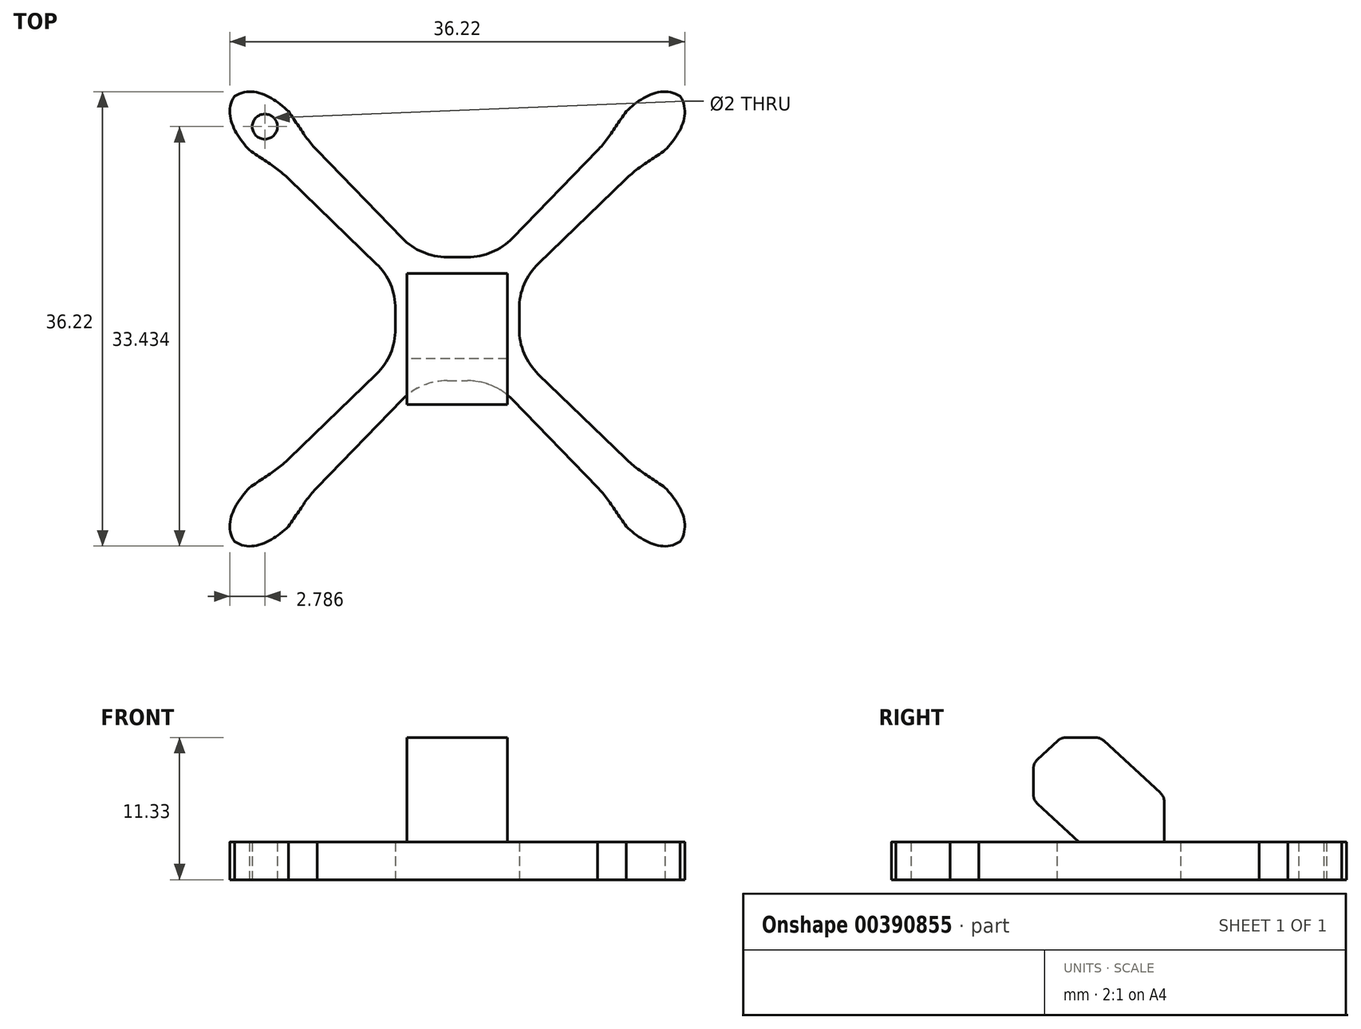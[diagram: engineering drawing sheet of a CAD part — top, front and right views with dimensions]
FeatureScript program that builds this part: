
annotation { "Feature Type Name" : "Feature", "Feature Type Description" : "" }
export const myFeature = defineFeature(function(context is Context, id is Id, definition is map)
    precondition{}
    {
        {
            var Q0;
            Q0=qCreatedBy(makeId("Top.planeOp"),FACE);
            var sketch = newSketch(context, id + "F0", { "sketchPlane" : qUnion([Q0])});
            skLineSegment(sketch, "E0.bottom", {"start": v(-17, -17) * mm, "end": v(17, -17) * mm, "construction": true});
            skLineSegment(sketch, "E0.top", {"start": v(-17, 17) * mm, "end": v(17, 17) * mm, "construction": true});
            skLineSegment(sketch, "E0.left", {"start": v(-17, -17) * mm, "end": v(-17, 17) * mm, "construction": true});
            skLineSegment(sketch, "E0.right", {"start": v(17, -17) * mm, "end": v(17, 17) * mm, "construction": true});
            skPoint(sketch, "E0.middle", {"position": v(0, 0) * mm});
            skLineSegment(sketch, "E1", {"start": v(-17, 17) * mm, "end": v(17, -17) * mm, "construction": true});
            skLineSegment(sketch, "E2", {"start": v(-17, -17) * mm, "end": v(17, 17) * mm, "construction": true});
            skLineSegment(sketch, "E3.bottom", {"start": v(-2.92, -4.92) * mm, "end": v(2.92, -4.92) * mm});
            skLineSegment(sketch, "E3.top", {"start": v(-2.92, 4.92) * mm, "end": v(2.92, 4.92) * mm});
            skLineSegment(sketch, "E3.left", {"start": v(-4.92, -2.92) * mm, "end": v(-4.92, 2.92) * mm});
            skLineSegment(sketch, "E3.right", {"start": v(4.92, -2.92) * mm, "end": v(4.92, 2.92) * mm});
            skPoint(sketch, "E4.visualSharp", {"position": v(-4.92, 4.92) * mm});
            skArc(sketch, "E4.filletArc", {"start": v(-2.92, 4.92) * mm, "mid": v(-4.34, 4.34) * mm, "end": v(-4.92, 2.92) * mm});
            skPoint(sketch, "E5.visualSharp", {"position": v(-4.92, -4.92) * mm});
            skArc(sketch, "E5.filletArc", {"start": v(-4.92, -2.92) * mm, "mid": v(-4.34, -4.34) * mm, "end": v(-2.92, -4.92) * mm});
            skPoint(sketch, "E6.visualSharp", {"position": v(4.92, -4.92) * mm});
            skArc(sketch, "E6.filletArc", {"start": v(2.92, -4.92) * mm, "mid": v(4.34, -4.34) * mm, "end": v(4.92, -2.92) * mm});
            skPoint(sketch, "E7.visualSharp", {"position": v(4.92, 4.92) * mm});
            skArc(sketch, "E7.filletArc", {"start": v(4.92, 2.92) * mm, "mid": v(4.34, 4.34) * mm, "end": v(2.92, 4.92) * mm});
            skFitSpline(sketch, "E8", {"points": [v(-16.54, 13.45) * mm, v(-17.74, 17.74) * mm], "startDerivative": vector(-3.26, 3.48) * mm, "endDerivative": vector(2.86, 4.37) * mm});
            skFitSpline(sketch, "E9.MirrorCS", {"points": [v(-13.45, 16.54) * mm, v(-17.74, 17.74) * mm], "startDerivative": vector(-3.48, 3.26) * mm, "endDerivative": vector(-4.37, -2.86) * mm});
            skFitSpline(sketch, "E10", {"points": [v(-13.45, 16.54) * mm, v(-11.15, 13.42) * mm], "startDerivative": vector(2.55, -3.63) * mm, "endDerivative": vector(2.55, -2.55) * mm});
            skLineSegment(sketch, "E11", {"start": v(-11.15, 13.42) * mm, "end": v(-2.92, 4.92) * mm});
            skLineSegment(sketch, "E12.MirrorCS", {"start": v(-13.42, 11.15) * mm, "end": v(-4.92, 2.92) * mm});
            skFitSpline(sketch, "E13.MirrorCS", {"points": [v(-16.54, 13.45) * mm, v(-13.42, 11.15) * mm], "startDerivative": vector(3.63, -2.55) * mm, "endDerivative": vector(2.55, -2.55) * mm});
            skLineSegment(sketch, "E14.MirrorCS", {"start": v(11.15, 13.42) * mm, "end": v(2.92, 4.92) * mm});
            skLineSegment(sketch, "E15.MirrorCS", {"start": v(13.42, 11.15) * mm, "end": v(4.92, 2.92) * mm});
            skFitSpline(sketch, "E16.MirrorCS", {"points": [v(13.45, 16.54) * mm, v(11.15, 13.42) * mm], "startDerivative": vector(-2.55, -3.63) * mm, "endDerivative": vector(-2.55, -2.55) * mm});
            skFitSpline(sketch, "E17.MirrorCS", {"points": [v(16.54, 13.45) * mm, v(13.42, 11.15) * mm], "startDerivative": vector(-3.63, -2.55) * mm, "endDerivative": vector(-2.55, -2.55) * mm});
            skFitSpline(sketch, "E18.MirrorCS", {"points": [v(16.54, 13.45) * mm, v(17.74, 17.74) * mm], "startDerivative": vector(3.26, 3.48) * mm, "endDerivative": vector(-2.86, 4.37) * mm});
            skFitSpline(sketch, "E19.MirrorCS", {"points": [v(13.45, 16.54) * mm, v(17.74, 17.74) * mm], "startDerivative": vector(3.48, 3.26) * mm, "endDerivative": vector(4.37, -2.86) * mm});
            skLineSegment(sketch, "E20.MirrorCS", {"start": v(-11.15, -13.42) * mm, "end": v(-2.92, -4.92) * mm});
            skLineSegment(sketch, "E21.MirrorCS", {"start": v(-13.42, -11.15) * mm, "end": v(-4.92, -2.92) * mm});
            skLineSegment(sketch, "E22.MirrorCS", {"start": v(11.15, -13.42) * mm, "end": v(2.92, -4.92) * mm});
            skLineSegment(sketch, "E23.MirrorCS", {"start": v(13.42, -11.15) * mm, "end": v(4.92, -2.92) * mm});
            skFitSpline(sketch, "E24.MirrorCS", {"points": [v(-16.54, -13.45) * mm, v(-13.42, -11.15) * mm], "startDerivative": vector(3.63, 2.55) * mm, "endDerivative": vector(2.55, 2.55) * mm});
            skFitSpline(sketch, "E25.MirrorCS", {"points": [v(-13.45, -16.54) * mm, v(-11.15, -13.42) * mm], "startDerivative": vector(2.55, 3.63) * mm, "endDerivative": vector(2.55, 2.55) * mm});
            skFitSpline(sketch, "E26.MirrorCS", {"points": [v(-16.54, -13.45) * mm, v(-17.74, -17.74) * mm], "startDerivative": vector(-3.26, -3.48) * mm, "endDerivative": vector(2.86, -4.37) * mm});
            skFitSpline(sketch, "E27.MirrorCS", {"points": [v(-13.45, -16.54) * mm, v(-17.74, -17.74) * mm], "startDerivative": vector(-3.48, -3.26) * mm, "endDerivative": vector(-4.37, 2.86) * mm});
            skFitSpline(sketch, "E28.MirrorCS", {"points": [v(13.45, -16.54) * mm, v(11.15, -13.42) * mm], "startDerivative": vector(-2.55, 3.63) * mm, "endDerivative": vector(-2.55, 2.55) * mm});
            skFitSpline(sketch, "E29.MirrorCS", {"points": [v(13.45, -16.54) * mm, v(17.74, -17.74) * mm], "startDerivative": vector(3.48, -3.26) * mm, "endDerivative": vector(4.37, 2.86) * mm});
            skFitSpline(sketch, "E30.MirrorCS", {"points": [v(16.54, -13.45) * mm, v(13.42, -11.15) * mm], "startDerivative": vector(-3.63, 2.55) * mm, "endDerivative": vector(-2.55, 2.55) * mm});
            skFitSpline(sketch, "E31.MirrorCS", {"points": [v(16.54, -13.45) * mm, v(17.74, -17.74) * mm], "startDerivative": vector(3.26, -3.48) * mm, "endDerivative": vector(-2.86, -4.37) * mm});
            skLineSegment(sketch, "E32.MirrorCS", {"start": v(17, 17) * mm, "end": v(17, -17) * mm, "construction": true});
            skCircle(sketch, "E33", {"center": v(-15.32, 15.32) * mm, "radius": 1 * mm});
            skSolve(sketch);
        }
        {
            var Q0;
            Q0 = qSketchRegion(id + "F0", true);
            extrude(context, id + "F1", {"entities" : qUnion([Q0]), "depth" : 3 * mm, "offsetDistance" : 25 * mm});
        }
        {
            var Q0;
            Q0=qCreatedBy(makeId("Right.planeOp"),FACE);
            var sketch = newSketch(context, id + "F2", { "sketchPlane" : qUnion([Q0])});
            skPoint(sketch, "E34.middle", {"position": v(0, 0) * mm});
            skPoint(sketch, "E34.bottom.end.orphan", {"position": v(4.92, -5) * mm});
            skPoint(sketch, "E34.bottom.start.orphan", {"position": v(-4.92, -5) * mm});
            skLineSegment(sketch, "E35.top", {"start": v(-3.16, 2.98) * mm, "end": v(3.61, 2.98) * mm});
            skLineSegment(sketch, "E36", {"start": v(3.61, 2.98) * mm, "end": v(3.61, 6.2) * mm});
            skLineSegment(sketch, "E37", {"start": v(3.29, 6.93) * mm, "end": v(-1.2, 11.07) * mm});
            skLineSegment(sketch, "E38", {"start": v(-1.88, 11.33) * mm, "end": v(-4.2, 11.33) * mm});
            skLineSegment(sketch, "E39", {"start": v(-4.87, 11.07) * mm, "end": v(-6.49, 9.57) * mm});
            skLineSegment(sketch, "E40", {"start": v(-6.8, 8.84) * mm, "end": v(-6.8, 6.8) * mm});
            skLineSegment(sketch, "E41", {"start": v(-6.49, 6.06) * mm, "end": v(-3.16, 2.98) * mm});
            skPoint(sketch, "E42.visualSharp", {"position": v(-6.8, 6.35) * mm});
            skArc(sketch, "E42.filletArc", {"start": v(-6.8, 6.8) * mm, "mid": v(-6.72, 6.39) * mm, "end": v(-6.49, 6.06) * mm});
            skPoint(sketch, "E43.visualSharp", {"position": v(-6.8, 9.28) * mm});
            skArc(sketch, "E43.filletArc", {"start": v(-6.49, 9.57) * mm, "mid": v(-6.72, 9.24) * mm, "end": v(-6.8, 8.84) * mm});
            skPoint(sketch, "E44.visualSharp", {"position": v(-4.59, 11.33) * mm});
            skArc(sketch, "E44.filletArc", {"start": v(-4.2, 11.33) * mm, "mid": v(-4.56, 11.26) * mm, "end": v(-4.87, 11.07) * mm});
            skPoint(sketch, "E45.visualSharp", {"position": v(-1.49, 11.33) * mm});
            skArc(sketch, "E45.filletArc", {"start": v(-1.2, 11.07) * mm, "mid": v(-1.51, 11.26) * mm, "end": v(-1.88, 11.33) * mm});
            skPoint(sketch, "E46.visualSharp", {"position": v(3.61, 6.63) * mm});
            skArc(sketch, "E46.filletArc", {"start": v(3.61, 6.2) * mm, "mid": v(3.53, 6.6) * mm, "end": v(3.29, 6.93) * mm});
            skPoint(sketch, "E47.orphan", {"position": v(-5.45, 2.98) * mm});
            skPoint(sketch, "E48.orphan", {"position": v(4.4, 2.98) * mm});
            skSolve(sketch);
        }
        {
            var Q0;
            Q0=makeQuery(id+"F2.imprint","IMPRINT",FACE,{"disambiguationData":[TD([[makeQuery(id+"F2.imprint","IMPRINT",EDGE,{"derivedFrom":sQuery(id+"F2.wireOp",EDGE,"E35.top")}),1.0]])]});
            extrude(context, id + "F3", {"entities" : qUnion([Q0]), "operationType" : NewBodyOperationType.ADD, "depth" : 4 * mm, "offsetDistance" : 25 * mm, "hasSecondDirection" : true, "secondDirectionOppositeDirection" : true, "secondDirectionDepth" : 4 * mm});
        }
        {
            var Q0;
            Q0=makeQuery(id+"F1.opExtrude","SWEPT_EDGE",EDGE,{"disambiguationData":[OSD([sQuery(id+"F0.wireOp",EDGE,"E3.right"),sQuery(id+"F0.wireOp",EDGE,"E6.filletArc"),sQuery(id+"F0.wireOp",EDGE,"E23.MirrorCS")])]});
            var Q1;
            Q1=makeQuery(id+"F1.opExtrude","SWEPT_EDGE",EDGE,{"disambiguationData":[OSD([sQuery(id+"F0.wireOp",EDGE,"E3.right"),sQuery(id+"F0.wireOp",EDGE,"E7.filletArc"),sQuery(id+"F0.wireOp",EDGE,"E15.MirrorCS")])]});
            var Q2;
            Q2=makeQuery(id+"F1.opExtrude","SWEPT_EDGE",EDGE,{"disambiguationData":[OSD([sQuery(id+"F0.wireOp",EDGE,"E3.top"),sQuery(id+"F0.wireOp",EDGE,"E7.filletArc"),sQuery(id+"F0.wireOp",EDGE,"E14.MirrorCS")])]});
            var Q3;
            Q3=makeQuery(id+"F1.opExtrude","SWEPT_EDGE",EDGE,{"disambiguationData":[OSD([sQuery(id+"F0.wireOp",EDGE,"E3.top"),sQuery(id+"F0.wireOp",EDGE,"E4.filletArc"),sQuery(id+"F0.wireOp",EDGE,"E11")])]});
            var Q4;
            Q4=makeQuery(id+"F1.opExtrude","SWEPT_EDGE",EDGE,{"disambiguationData":[OSD([sQuery(id+"F0.wireOp",EDGE,"E3.left"),sQuery(id+"F0.wireOp",EDGE,"E4.filletArc"),sQuery(id+"F0.wireOp",EDGE,"E12.MirrorCS")])]});
            var Q5;
            Q5=makeQuery(id+"F1.opExtrude","SWEPT_EDGE",EDGE,{"disambiguationData":[OSD([sQuery(id+"F0.wireOp",EDGE,"E3.left"),sQuery(id+"F0.wireOp",EDGE,"E5.filletArc"),sQuery(id+"F0.wireOp",EDGE,"E21.MirrorCS")])]});
            var Q6;
            Q6=makeQuery(id+"F1.opExtrude","SWEPT_EDGE",EDGE,{"disambiguationData":[OSD([sQuery(id+"F0.wireOp",EDGE,"E3.bottom"),sQuery(id+"F0.wireOp",EDGE,"E5.filletArc"),sQuery(id+"F0.wireOp",EDGE,"E20.MirrorCS")])]});
            var Q7;
            Q7=makeQuery(id+"F1.opExtrude","SWEPT_EDGE",EDGE,{"disambiguationData":[OSD([sQuery(id+"F0.wireOp",EDGE,"E3.bottom"),sQuery(id+"F0.wireOp",EDGE,"E6.filletArc"),sQuery(id+"F0.wireOp",EDGE,"E22.MirrorCS")])]});
            fillet(context, id + "F4", {"entities" : qUnion([Q0, Q1, Q2, Q3, Q4, Q5, Q6, Q7]), "radius" : 5 * mm, "tangentPropagation" : true, "allowEdgeOverflow" : false});
        }
    });
